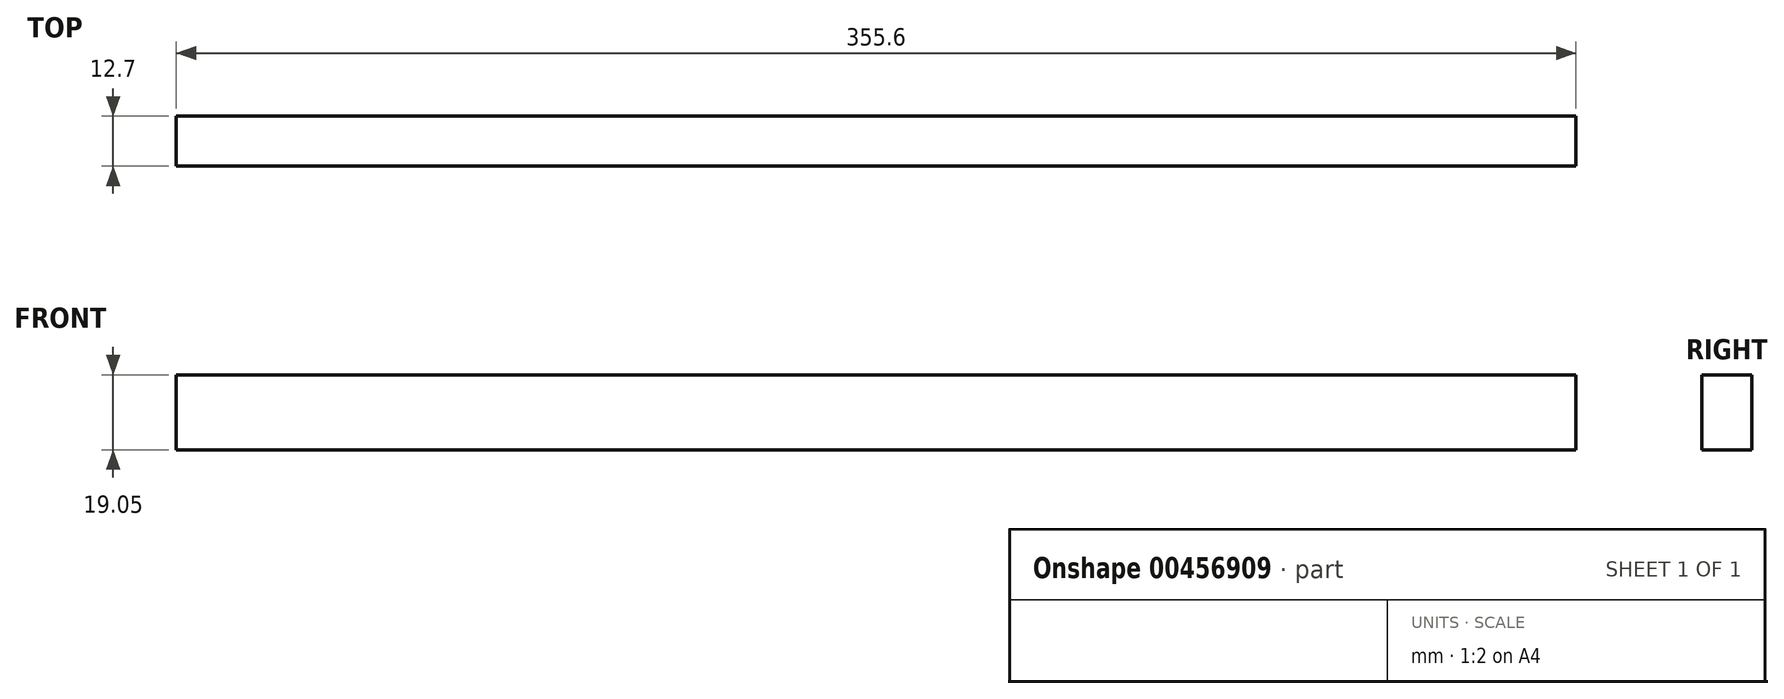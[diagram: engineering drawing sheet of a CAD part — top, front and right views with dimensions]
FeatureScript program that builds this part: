
annotation { "Feature Type Name" : "Feature", "Feature Type Description" : "" }
export const myFeature = defineFeature(function(context is Context, id is Id, definition is map)
    precondition{}
    {
        {
            var Q0;
            Q0=qCreatedBy(makeId("Front.planeOp"),FACE);
            var sketch = newSketch(context, id + "F0", { "sketchPlane" : qUnion([Q0])});
            skLineSegment(sketch, "E0.bottom", {"start": v(294.64, 154.51) * mm, "end": v(294.64, 135.46) * mm});
            skLineSegment(sketch, "E0.top", {"start": v(-60.96, 154.51) * mm, "end": v(-60.96, 135.46) * mm});
            skLineSegment(sketch, "E0.left", {"start": v(294.64, 154.51) * mm, "end": v(-60.96, 154.51) * mm});
            skLineSegment(sketch, "E0.right", {"start": v(294.64, 135.46) * mm, "end": v(-60.96, 135.46) * mm});
            skSolve(sketch);
        }
        {
            var Q0;
            Q0=makeQuery(id+"F0.imprint","IMPRINT",FACE,{"disambiguationData":[TD([[makeQuery(id+"F0.imprint","IMPRINT",EDGE,{"derivedFrom":sQuery(id+"F0.wireOp",EDGE,"CR0fLDGC-FUSB-T87a-WjLq-PKh2d8LQHOZw.bottom")}),-1.0]])]});
            var Q1;
            Q1=makeQuery(id+"F0.imprint","IMPRINT",FACE,{"disambiguationData":[TD([[makeQuery(id+"F0.imprint","IMPRINT",EDGE,{"derivedFrom":sQuery(id+"F0.wireOp",EDGE,"E0.bottom")}),-1.0]])]});
            extrude(context, id + "F1", {"entities" : qUnion([Q0, Q1]), "depth" : 12.7 * mm});
        }
    });
